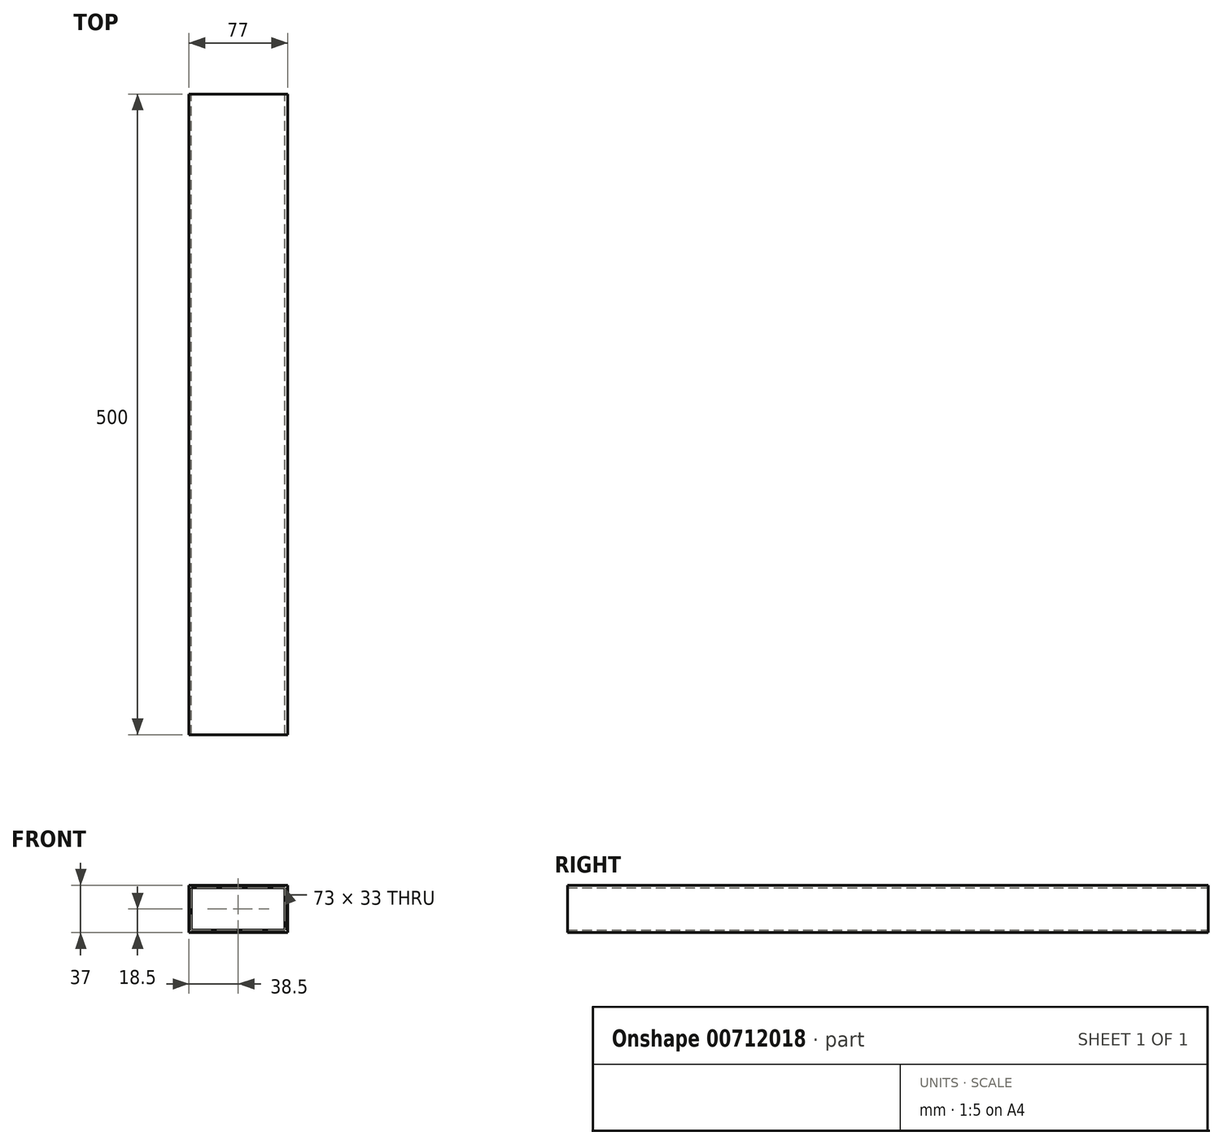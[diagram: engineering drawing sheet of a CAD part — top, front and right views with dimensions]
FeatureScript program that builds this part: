
annotation { "Feature Type Name" : "Feature", "Feature Type Description" : "" }
export const myFeature = defineFeature(function(context is Context, id is Id, definition is map)
    precondition{}
    {
        {
            var Q0;
            Q0=qCreatedBy(makeId("Front.planeOp"),FACE);
            var sketch = newSketch(context, id + "F0", { "sketchPlane" : qUnion([Q0])});
            skLineSegment(sketch, "E0.bottom", {"start": v(0, 0) * mm, "end": v(77, 0) * mm});
            skLineSegment(sketch, "E0.top", {"start": v(0, -37) * mm, "end": v(77, -37) * mm});
            skLineSegment(sketch, "E0.left", {"start": v(0, 0) * mm, "end": v(0, -37) * mm});
            skLineSegment(sketch, "E0.right", {"start": v(77, 0) * mm, "end": v(77, -37) * mm});
            skLineSegment(sketch, "E1.0", {"start": v(2, -2) * mm, "end": v(75, -2) * mm});
            skLineSegment(sketch, "E1.1", {"start": v(2, -2) * mm, "end": v(2, -35) * mm});
            skLineSegment(sketch, "E1.2", {"start": v(2, -35) * mm, "end": v(75, -35) * mm});
            skLineSegment(sketch, "E1.3", {"start": v(75, -2) * mm, "end": v(75, -35) * mm});
            skSolve(sketch);
        }
        {
            var Q0;
            Q0 = qSketchRegion(id + "F0", true);
            extrude(context, id + "F1", {"entities" : qUnion([Q0]), "depth" : 500 * mm, "offsetDistance" : 25 * mm});
        }
    });
